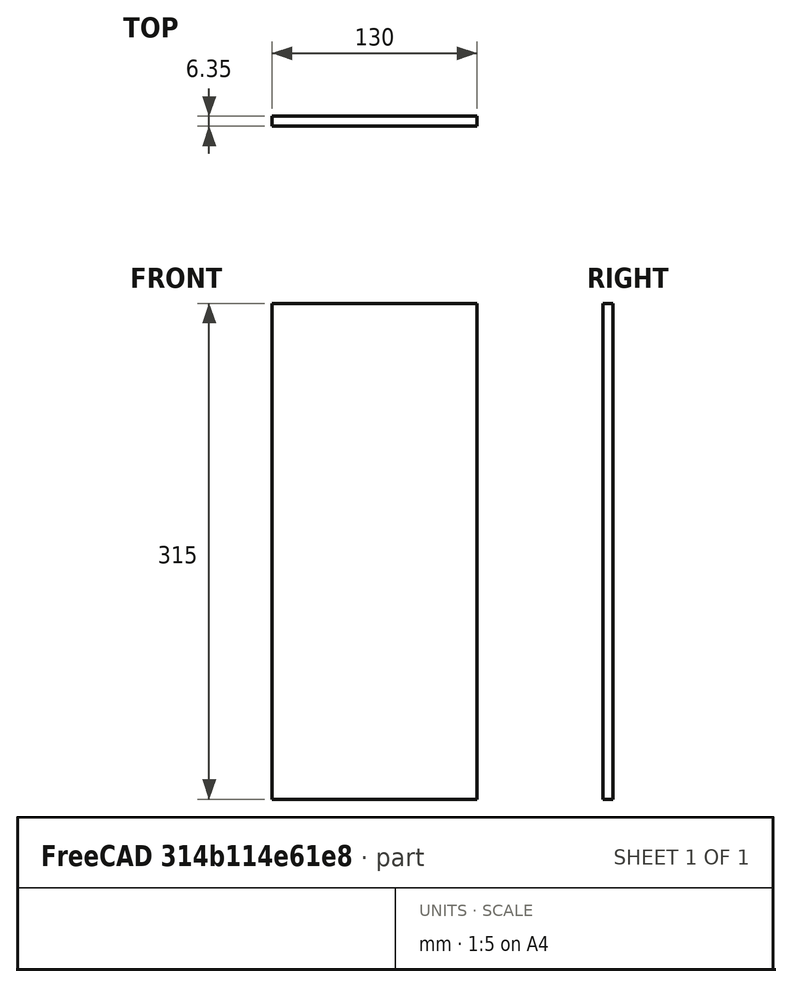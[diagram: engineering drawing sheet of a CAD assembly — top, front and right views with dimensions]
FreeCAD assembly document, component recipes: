
FREECAD ASSEMBLY — COMPONENT RECIPES ("Integrated PiTrac")

This assembly document has 13 components, labeled P0..P12 below (a component is one placed body or linked part). 1 of them carries a construction recipe — the FreeCAD feature program that regenerates the part from scratch, quoted from this document or its linked companion documents; the rest are supplied as boundary geometry only. No exploded tour is included for this assembly.
COMPONENT P0 — geometry summary ("p2AP-PCBModel"; no construction recipe available for this part):
  bounding box: 231.5 x 110.4 x 36.9 mm
  tessellated surface: 635,688 triangles
  volume: 60856 mm^3 (6% of its bounding box)
COMPONENT P1 — geometry summary ("Tower Part"; no construction recipe available for this part):
  bounding box: 264.0 x 127.6 x 114.7 mm
  tessellated surface: 27,334 triangles
  volume: 270391 mm^3 (7% of its bounding box)
COMPONENT P2 — geometry summary ("Botom Camera Mount Object"; no construction recipe available for this part):
  bounding box: 66.0 x 51.4 x 30.4 mm
  tessellated surface: 7,484 triangles
  volume: 25588 mm^3 (25% of its bounding box)
COMPONENT P3 — geometry summary ("LED Light Mount Object"; no construction recipe available for this part):
  bounding box: 88.0 x 73.3 x 33.2 mm
  tessellated surface: 9,100 triangles
  volume: 41281 mm^3 (19% of its bounding box)
  symmetry: mirror-symmetric across its x mid-plane
COMPONENT P4 — geometry summary ("Bottom Raspberry Pi HQ Camera with cs mount lens v014"; no construction recipe available for this part):
  bounding box: 56.5 x 51.3 x 38.0 mm
  tessellated surface: 88,684 triangles
  volume: 25722 mm^3 (23% of its bounding box)
  symmetry: mirror-symmetric across its x mid-plane
COMPONENT P5 — geometry summary ("Camera Mount - Top Object"; no construction recipe available for this part):
  bounding box: 73.6 x 66.0 x 33.6 mm
  tessellated surface: 7,476 triangles
  volume: 28146 mm^3 (17% of its bounding box)
COMPONENT P6 — geometry summary ("Raspberry Pi HQ Camera with cs mount lens v014"; no construction recipe available for this part):
  bounding box: 62.4 x 58.2 x 38.0 mm
  tessellated surface: 88,684 triangles
  volume: 25722 mm^3 (19% of its bounding box)
  symmetry: mirror-symmetric across its x mid-plane
COMPONENT P7 — geometry summary ("Filter Holder Part"; no construction recipe available for this part):
  bounding box: 37.5 x 36.5 x 22.7 mm
  tessellated surface: 4,272 triangles
  volume: 4979 mm^3 (16% of its bounding box)
COMPONENT P8 — geometry summary ("BaseBox Part"; no construction recipe available for this part):
  bounding box: 200.1 x 200.0 x 70.0 mm
  tessellated surface: 30,692 triangles
  volume: 490740 mm^3 (18% of its bounding box)
COMPONENT P9 — geometry summary ("LRS-154"; no construction recipe available for this part):
  bounding box: 159.0 x 97.0 x 30.0 mm
  tessellated surface: 81,829 triangles
  volume: 73054 mm^3 (16% of its bounding box)
COMPONENT P10 — geometry summary ("JR-101-1F008"; no construction recipe available for this part):
  bounding box: 44.0 x 33.0 x 27.7 mm
  tessellated surface: 13,740 triangles
  volume: 8508 mm^3 (21% of its bounding box)
COMPONENT P11 — geometry summary ("Case Cover Part"; no construction recipe available for this part):
  bounding box: 266.1 x 126.0 x 124.6 mm
  tessellated surface: 10,752 triangles
  volume: 308885 mm^3 (7% of its bounding box)
  symmetry: mirror-symmetric across its x mid-plane
COMPONENT P12 — recipe-attached ("Shank Shield Part", modeled in this document).
Construction recipe (the document's own serialized feature program — sketch geometry with constraints, then the solid features built on it; lengths are millimeters unless a unit is written):

FEATURE [Sketcher::SketchObject] Sketch  label="Shank Shield Sketch"
  ArcFitTolerance = 1e-06
  AttachmentSupport = -> [XZ_Plane002]
  FullyConstrained = false
  MakeInternals = false
  MapMode = 5
  Placement = pos=(0,0,0) rot=(1,0,0;1.5708rad)
  expr: Constraints[8] = <<Monitor Chassis Parameters>>.GSShankShieldWidth
  expr: Constraints[9] = <<Monitor Chassis Parameters>>.GSShankShieldHeight
  sketch-geometry (4):
    g0: LineSegment StartX=68.4149 StartY=-76.5925 StartZ=0 EndX=68.4149 EndY=238.407 EndZ=0
    g1: LineSegment StartX=68.4149 StartY=238.407 StartZ=0 EndX=-61.5851 EndY=238.407 EndZ=0
    g2: LineSegment StartX=-61.5851 StartY=238.407 StartZ=0 EndX=-61.5851 EndY=-76.5925 EndZ=0
    g3: LineSegment StartX=-61.5851 StartY=-76.5925 StartZ=0 EndX=68.4149 EndY=-76.5925 EndZ=0
  constraints (10):
    c: Coincident(g0,g1)
    c: Coincident(g1,g2)
    c: Coincident(g2,g3)
    c: Coincident(g3,g0)
    c: Vertical(g0)
    c: Vertical(g2)
    c: Horizontal(g1)
    c: Horizontal(g3)
    c: DistanceX(g1,g0) = 130
    c: DistanceY(g0,g0) = 315
FEATURE [PartDesign::Pad] Pad  label="Shank Shield Pad"
  Direction = (0,-1,2e-16)
  Length = 6.35
  Length2 = 10
  Placement = pos=(0,0,0) rot=(1,0,0;1.5708rad)
  Profile = -> Sketch
  ReferenceAxis = -> Sketch [N_Axis]
  Suppressed = false
  Type = 0
  expr: Length = <<Monitor Chassis Parameters>>.GSShankShieldThickness
FEATURE [PartDesign::Body] Body  label="Shank Shield Body"
  AllowCompound = false
  Group = -> [Sketch,Pad]
  Origin = -> Origin002
  Tip = -> Pad
PROVENANCE & LICENSES
A FreeCAD (.FCStd) document from a public repository crawl; recipes are the document's own serialized feature recipes (and, for linked parts, companion documents' recipes).
License: gpl-2.0.
